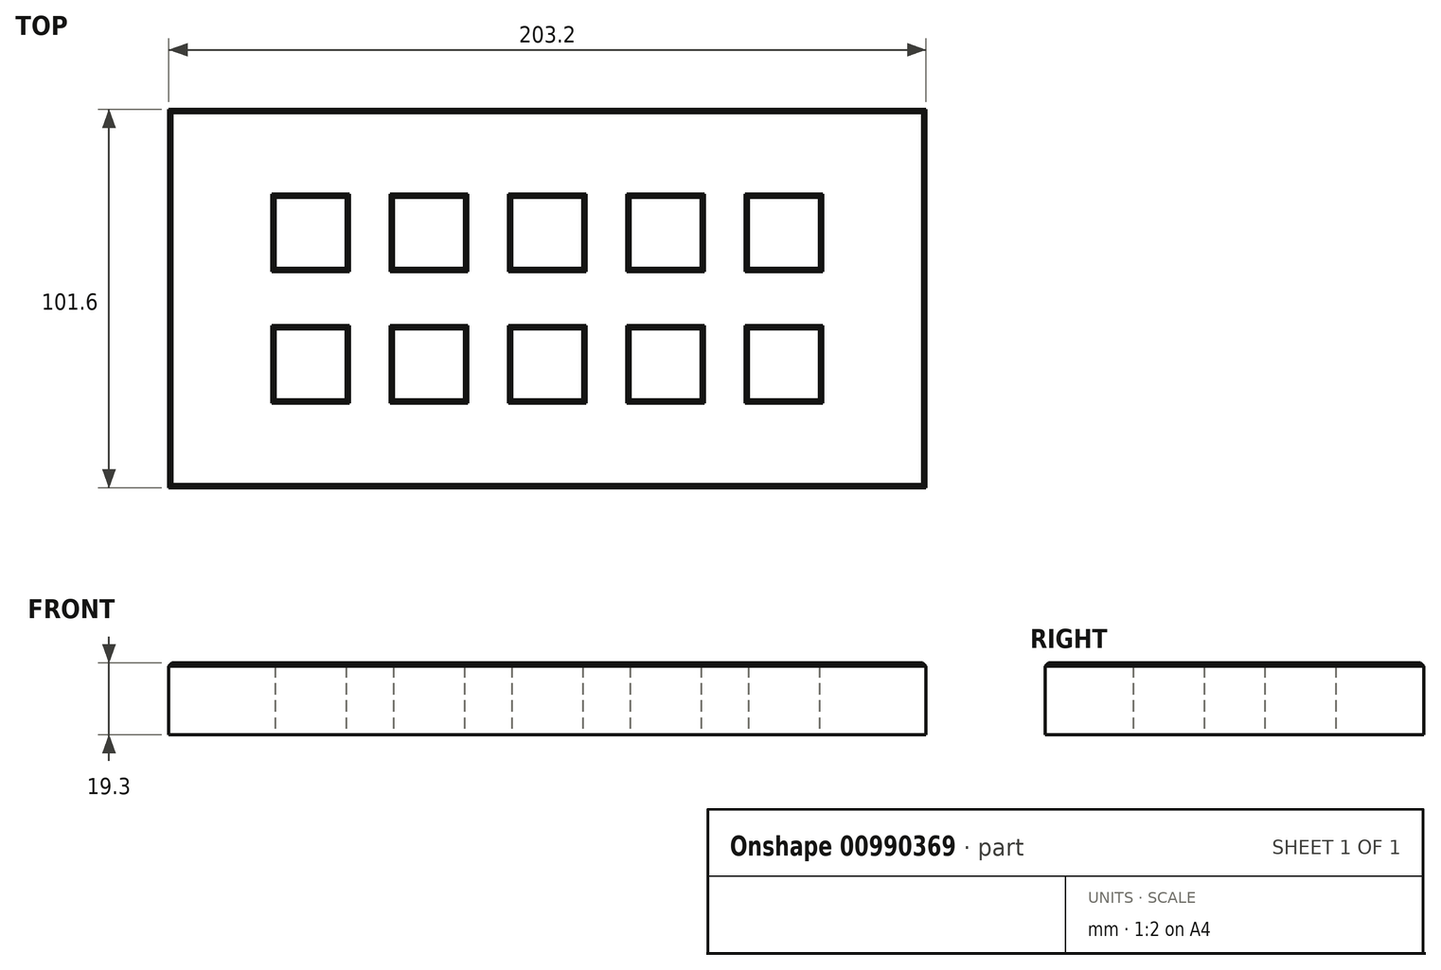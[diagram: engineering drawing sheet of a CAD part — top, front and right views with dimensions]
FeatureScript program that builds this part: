
annotation { "Feature Type Name" : "Feature", "Feature Type Description" : "" }
export const myFeature = defineFeature(function(context is Context, id is Id, definition is map)
    precondition{}
    {
        {
            var Q0;
            Q0=qCreatedBy(makeId("Top.planeOp"),FACE);
            var sketch = newSketch(context, id + "F0", { "sketchPlane" : qUnion([Q0])});
            skLineSegment(sketch, "E0.bottom", {"start": v(-101.6, 50.8) * mm, "end": v(101.6, 50.8) * mm});
            skLineSegment(sketch, "E0.top", {"start": v(-101.6, -50.8) * mm, "end": v(101.6, -50.8) * mm});
            skLineSegment(sketch, "E0.left", {"start": v(-101.6, 50.8) * mm, "end": v(-101.6, -50.8) * mm});
            skLineSegment(sketch, "E0.right", {"start": v(101.6, 50.8) * mm, "end": v(101.6, -50.8) * mm});
            skPoint(sketch, "E0.middle", {"position": v(0, 0) * mm});
            skLineSegment(sketch, "E1.bottom", {"start": v(-73.02, 27.17) * mm, "end": v(-53.98, 27.17) * mm});
            skLineSegment(sketch, "E1.top", {"start": v(-73.02, 8.12) * mm, "end": v(-53.97, 8.12) * mm});
            skLineSegment(sketch, "E1.left", {"start": v(-73.02, 27.17) * mm, "end": v(-73.02, 8.12) * mm});
            skLineSegment(sketch, "E1.right", {"start": v(-53.98, 27.17) * mm, "end": v(-53.97, 8.12) * mm});
            skPoint(sketch, "E1.middle", {"position": v(-63.5, 17.65) * mm});
            skLineSegment(sketch, "E2.bottom", {"start": v(-41.27, 8.12) * mm, "end": v(-22.22, 8.12) * mm});
            skLineSegment(sketch, "E2.top", {"start": v(-41.27, 27.17) * mm, "end": v(-22.22, 27.17) * mm});
            skLineSegment(sketch, "E2.left", {"start": v(-41.27, 8.12) * mm, "end": v(-41.27, 27.17) * mm});
            skLineSegment(sketch, "E2.right", {"start": v(-22.22, 8.12) * mm, "end": v(-22.22, 27.17) * mm});
            skLineSegment(sketch, "E3.bottom", {"start": v(-9.52, 8.12) * mm, "end": v(9.53, 8.12) * mm});
            skLineSegment(sketch, "E3.top", {"start": v(-9.52, 27.17) * mm, "end": v(9.53, 27.17) * mm});
            skLineSegment(sketch, "E3.left", {"start": v(-9.52, 8.12) * mm, "end": v(-9.52, 27.17) * mm});
            skLineSegment(sketch, "E3.right", {"start": v(9.53, 8.12) * mm, "end": v(9.53, 27.17) * mm});
            skLineSegment(sketch, "E4.bottom", {"start": v(22.23, 8.12) * mm, "end": v(41.28, 8.12) * mm});
            skLineSegment(sketch, "E4.top", {"start": v(22.23, 27.17) * mm, "end": v(41.28, 27.17) * mm});
            skLineSegment(sketch, "E4.left", {"start": v(22.23, 8.12) * mm, "end": v(22.23, 27.17) * mm});
            skLineSegment(sketch, "E4.right", {"start": v(41.28, 8.12) * mm, "end": v(41.28, 27.17) * mm});
            skLineSegment(sketch, "E5.bottom", {"start": v(53.98, 8.12) * mm, "end": v(73.03, 8.12) * mm});
            skLineSegment(sketch, "E5.top", {"start": v(53.98, 27.17) * mm, "end": v(73.03, 27.17) * mm});
            skLineSegment(sketch, "E5.left", {"start": v(53.98, 8.12) * mm, "end": v(53.98, 27.17) * mm});
            skLineSegment(sketch, "E5.right", {"start": v(73.03, 8.12) * mm, "end": v(73.03, 27.17) * mm});
            skLineSegment(sketch, "E6", {"start": v(0, 0) * mm, "end": v(-101.6, 0) * mm, "construction": true});
            skPoint(sketch, "E7", {"position": v(0, 27.17) * mm});
            skPoint(sketch, "E8", {"position": v(0, 50.8) * mm});
            skPoint(sketch, "E9.MirrorP", {"position": v(0, -27.17) * mm});
            skLineSegment(sketch, "E10.MirrorCS", {"start": v(-73.02, -27.17) * mm, "end": v(-53.98, -27.17) * mm});
            skLineSegment(sketch, "E11.MirrorCS", {"start": v(-73.02, -27.17) * mm, "end": v(-73.02, -8.12) * mm});
            skLineSegment(sketch, "E12.MirrorCS", {"start": v(-73.02, -8.12) * mm, "end": v(-53.97, -8.12) * mm});
            skLineSegment(sketch, "E13.MirrorCS", {"start": v(-53.97, -27.17) * mm, "end": v(-53.97, -8.12) * mm});
            skLineSegment(sketch, "E14.MirrorCS", {"start": v(-41.27, -8.12) * mm, "end": v(-41.27, -27.17) * mm});
            skLineSegment(sketch, "E15.MirrorCS", {"start": v(-41.27, -27.17) * mm, "end": v(-22.22, -27.17) * mm});
            skLineSegment(sketch, "E16.MirrorCS", {"start": v(-22.22, -8.12) * mm, "end": v(-22.22, -27.17) * mm});
            skLineSegment(sketch, "E17.MirrorCS", {"start": v(-41.27, -8.12) * mm, "end": v(-22.22, -8.12) * mm});
            skLineSegment(sketch, "E18.MirrorCS", {"start": v(-9.52, -8.12) * mm, "end": v(-9.52, -27.17) * mm});
            skLineSegment(sketch, "E19.MirrorCS", {"start": v(-9.52, -27.17) * mm, "end": v(9.53, -27.17) * mm});
            skLineSegment(sketch, "E20.MirrorCS", {"start": v(9.53, -8.12) * mm, "end": v(9.53, -27.17) * mm});
            skLineSegment(sketch, "E21.MirrorCS", {"start": v(-9.52, -8.12) * mm, "end": v(9.53, -8.12) * mm});
            skLineSegment(sketch, "E22.MirrorCS", {"start": v(22.23, -8.12) * mm, "end": v(22.23, -27.17) * mm});
            skLineSegment(sketch, "E23.MirrorCS", {"start": v(22.23, -27.17) * mm, "end": v(41.28, -27.17) * mm});
            skLineSegment(sketch, "E24.MirrorCS", {"start": v(41.28, -8.12) * mm, "end": v(41.28, -27.17) * mm});
            skLineSegment(sketch, "E25.MirrorCS", {"start": v(22.23, -8.12) * mm, "end": v(41.28, -8.12) * mm});
            skLineSegment(sketch, "E26.MirrorCS", {"start": v(53.98, -8.12) * mm, "end": v(53.98, -27.17) * mm});
            skLineSegment(sketch, "E27.MirrorCS", {"start": v(53.98, -27.17) * mm, "end": v(73.03, -27.17) * mm});
            skLineSegment(sketch, "E28.MirrorCS", {"start": v(73.03, -8.12) * mm, "end": v(73.03, -27.17) * mm});
            skLineSegment(sketch, "E29.MirrorCS", {"start": v(53.98, -8.12) * mm, "end": v(73.03, -8.12) * mm});
            skSolve(sketch);
        }
        {
            var Q0;
            Q0=makeQuery(id+"F0.imprint","IMPRINT",FACE,{"disambiguationData":[TD([[makeQuery(id+"F0.imprint","IMPRINT",EDGE,{"derivedFrom":sQuery(id+"F0.wireOp",EDGE,"E0.bottom")}),-1.0]])]});
            extrude(context, id + "F1", {"entities" : qUnion([Q0]), "depth" : 19.3 * mm, "offsetDistance" : 25.4 * mm});
        }
        {
            var Q0;
            Q0=makeQuery(id+"F0.imprint","IMPRINT",FACE,{"disambiguationData":[TD([[makeQuery(id+"F0.imprint","IMPRINT",EDGE,{"derivedFrom":sQuery(id+"F0.wireOp",EDGE,"E1.bottom")}),-1.0]])]});
            var Q1;
            Q1=makeQuery(id+"F0.imprint","IMPRINT",FACE,{"disambiguationData":[TD([[makeQuery(id+"F0.imprint","IMPRINT",EDGE,{"derivedFrom":sQuery(id+"F0.wireOp",EDGE,"E2.bottom")}),1.0]])]});
            var Q2;
            Q2=makeQuery(id+"F0.imprint","IMPRINT",FACE,{"disambiguationData":[TD([[makeQuery(id+"F0.imprint","IMPRINT",EDGE,{"derivedFrom":sQuery(id+"F0.wireOp",EDGE,"E3.bottom")}),1.0]])]});
            var Q3;
            Q3=makeQuery(id+"F0.imprint","IMPRINT",FACE,{"disambiguationData":[TD([[makeQuery(id+"F0.imprint","IMPRINT",EDGE,{"derivedFrom":sQuery(id+"F0.wireOp",EDGE,"E4.bottom")}),1.0]])]});
            var Q4;
            Q4=makeQuery(id+"F0.imprint","IMPRINT",FACE,{"disambiguationData":[TD([[makeQuery(id+"F0.imprint","IMPRINT",EDGE,{"derivedFrom":sQuery(id+"F0.wireOp",EDGE,"E5.bottom")}),1.0]])]});
            var Q5;
            Q5=makeQuery(id+"F0.imprint","IMPRINT",FACE,{"disambiguationData":[TD([[makeQuery(id+"F0.imprint","IMPRINT",EDGE,{"derivedFrom":sQuery(id+"F0.wireOp",EDGE,"E26.MirrorCS")}),1.0]])]});
            var Q6;
            Q6=makeQuery(id+"F0.imprint","IMPRINT",FACE,{"disambiguationData":[TD([[makeQuery(id+"F0.imprint","IMPRINT",EDGE,{"derivedFrom":sQuery(id+"F0.wireOp",EDGE,"E22.MirrorCS")}),1.0]])]});
            var Q7;
            Q7=makeQuery(id+"F0.imprint","IMPRINT",FACE,{"disambiguationData":[TD([[makeQuery(id+"F0.imprint","IMPRINT",EDGE,{"derivedFrom":sQuery(id+"F0.wireOp",EDGE,"E18.MirrorCS")}),1.0]])]});
            var Q8;
            Q8=makeQuery(id+"F0.imprint","IMPRINT",FACE,{"disambiguationData":[TD([[makeQuery(id+"F0.imprint","IMPRINT",EDGE,{"derivedFrom":sQuery(id+"F0.wireOp",EDGE,"E14.MirrorCS")}),1.0]])]});
            var Q9;
            Q9=makeQuery(id+"F0.imprint","IMPRINT",FACE,{"disambiguationData":[TD([[makeQuery(id+"F0.imprint","IMPRINT",EDGE,{"derivedFrom":sQuery(id+"F0.wireOp",EDGE,"E10.MirrorCS")}),1.0]])]});
            extrude(context, id + "F2", {"entities" : qUnion([Q0, Q1, Q2, Q3, Q4, Q5, Q6, Q7, Q8, Q9]), "depth" : 19.3 * mm, "offsetDistance" : 25.4 * mm});
        }
        {
            var Q0;
            Q0=makeQuery(id+"F2.opExtrude","CAP_FACE",FACE,{"disambiguationData":[OSD([sQuery(id+"F0.wireOp",EDGE,"E1.bottom"),sQuery(id+"F0.wireOp",EDGE,"E1.top"),sQuery(id+"F0.wireOp",EDGE,"E1.left"),sQuery(id+"F0.wireOp",EDGE,"E1.right")])],"isStart":false});
            var Q1;
            Q1=makeQuery(id+"F2.opExtrude","CAP_FACE",FACE,{"disambiguationData":[OSD([sQuery(id+"F0.wireOp",EDGE,"E2.bottom"),sQuery(id+"F0.wireOp",EDGE,"E2.top"),sQuery(id+"F0.wireOp",EDGE,"E2.left"),sQuery(id+"F0.wireOp",EDGE,"E2.right")])],"isStart":false});
            var Q2;
            Q2=makeQuery(id+"F2.opExtrude","CAP_FACE",FACE,{"disambiguationData":[OSD([sQuery(id+"F0.wireOp",EDGE,"E3.bottom"),sQuery(id+"F0.wireOp",EDGE,"E3.top"),sQuery(id+"F0.wireOp",EDGE,"E3.left"),sQuery(id+"F0.wireOp",EDGE,"E3.right")])],"isStart":false});
            var Q3;
            Q3=makeQuery(id+"F2.opExtrude","CAP_FACE",FACE,{"disambiguationData":[OSD([sQuery(id+"F0.wireOp",EDGE,"E4.bottom"),sQuery(id+"F0.wireOp",EDGE,"E4.top"),sQuery(id+"F0.wireOp",EDGE,"E4.left"),sQuery(id+"F0.wireOp",EDGE,"E4.right")])],"isStart":false});
            var Q4;
            Q4=makeQuery(id+"F2.opExtrude","CAP_FACE",FACE,{"disambiguationData":[OSD([sQuery(id+"F0.wireOp",EDGE,"E5.bottom"),sQuery(id+"F0.wireOp",EDGE,"E5.top"),sQuery(id+"F0.wireOp",EDGE,"E5.left"),sQuery(id+"F0.wireOp",EDGE,"E5.right")])],"isStart":false});
            var Q5;
            Q5=makeQuery(id+"F2.opExtrude","CAP_FACE",FACE,{"disambiguationData":[OSD([sQuery(id+"F0.wireOp",EDGE,"E26.MirrorCS"),sQuery(id+"F0.wireOp",EDGE,"E27.MirrorCS"),sQuery(id+"F0.wireOp",EDGE,"E28.MirrorCS"),sQuery(id+"F0.wireOp",EDGE,"E29.MirrorCS")])],"isStart":false});
            var Q6;
            Q6=makeQuery(id+"F2.opExtrude","CAP_FACE",FACE,{"disambiguationData":[OSD([sQuery(id+"F0.wireOp",EDGE,"E22.MirrorCS"),sQuery(id+"F0.wireOp",EDGE,"E23.MirrorCS"),sQuery(id+"F0.wireOp",EDGE,"E24.MirrorCS"),sQuery(id+"F0.wireOp",EDGE,"E25.MirrorCS")])],"isStart":false});
            var Q7;
            Q7=makeQuery(id+"F2.opExtrude","CAP_FACE",FACE,{"disambiguationData":[OSD([sQuery(id+"F0.wireOp",EDGE,"E18.MirrorCS"),sQuery(id+"F0.wireOp",EDGE,"E19.MirrorCS"),sQuery(id+"F0.wireOp",EDGE,"E20.MirrorCS"),sQuery(id+"F0.wireOp",EDGE,"E21.MirrorCS")])],"isStart":false});
            var Q8;
            Q8=makeQuery(id+"F2.opExtrude","CAP_FACE",FACE,{"disambiguationData":[OSD([sQuery(id+"F0.wireOp",EDGE,"E14.MirrorCS"),sQuery(id+"F0.wireOp",EDGE,"E15.MirrorCS"),sQuery(id+"F0.wireOp",EDGE,"E16.MirrorCS"),sQuery(id+"F0.wireOp",EDGE,"E17.MirrorCS")])],"isStart":false});
            var Q9;
            Q9=makeQuery(id+"F2.opExtrude","CAP_FACE",FACE,{"disambiguationData":[OSD([sQuery(id+"F0.wireOp",EDGE,"E10.MirrorCS"),sQuery(id+"F0.wireOp",EDGE,"E11.MirrorCS"),sQuery(id+"F0.wireOp",EDGE,"E12.MirrorCS"),sQuery(id+"F0.wireOp",EDGE,"E13.MirrorCS")])],"isStart":false});
            extrude(context, id + "F3", {"entities" : qUnion([Q0, Q1, Q2, Q3, Q4, Q5, Q6, Q7, Q8, Q9]), "operationType" : NewBodyOperationType.REMOVE, "oppositeDirection" : true, "depth" : 0.89 * mm, "offsetDistance" : 25.4 * mm});
        }
        {
            var Q0;
            Q0=makeQuery(id+"F1.opExtrude","CAP_FACE",FACE,{"disambiguationData":[OSD([sQuery(id+"F0.wireOp",EDGE,"E0.bottom"),sQuery(id+"F0.wireOp",EDGE,"E0.top"),sQuery(id+"F0.wireOp",EDGE,"E0.left"),sQuery(id+"F0.wireOp",EDGE,"E0.right"),sQuery(id+"F0.wireOp",EDGE,"E1.bottom"),sQuery(id+"F0.wireOp",EDGE,"E1.top"),sQuery(id+"F0.wireOp",EDGE,"E1.left"),sQuery(id+"F0.wireOp",EDGE,"E1.right"),sQuery(id+"F0.wireOp",EDGE,"E2.bottom"),sQuery(id+"F0.wireOp",EDGE,"E2.top"),sQuery(id+"F0.wireOp",EDGE,"E2.left"),sQuery(id+"F0.wireOp",EDGE,"E2.right"),sQuery(id+"F0.wireOp",EDGE,"E3.bottom"),sQuery(id+"F0.wireOp",EDGE,"E3.top"),sQuery(id+"F0.wireOp",EDGE,"E3.left"),sQuery(id+"F0.wireOp",EDGE,"E3.right"),sQuery(id+"F0.wireOp",EDGE,"E4.bottom"),sQuery(id+"F0.wireOp",EDGE,"E4.top"),sQuery(id+"F0.wireOp",EDGE,"E4.left"),sQuery(id+"F0.wireOp",EDGE,"E4.right"),sQuery(id+"F0.wireOp",EDGE,"E5.bottom"),sQuery(id+"F0.wireOp",EDGE,"E5.top"),sQuery(id+"F0.wireOp",EDGE,"E5.left"),sQuery(id+"F0.wireOp",EDGE,"E5.right"),sQuery(id+"F0.wireOp",EDGE,"E10.MirrorCS"),sQuery(id+"F0.wireOp",EDGE,"E11.MirrorCS"),sQuery(id+"F0.wireOp",EDGE,"E12.MirrorCS"),sQuery(id+"F0.wireOp",EDGE,"E13.MirrorCS"),sQuery(id+"F0.wireOp",EDGE,"E14.MirrorCS"),sQuery(id+"F0.wireOp",EDGE,"E15.MirrorCS"),sQuery(id+"F0.wireOp",EDGE,"E16.MirrorCS"),sQuery(id+"F0.wireOp",EDGE,"E17.MirrorCS"),sQuery(id+"F0.wireOp",EDGE,"E18.MirrorCS"),sQuery(id+"F0.wireOp",EDGE,"E19.MirrorCS"),sQuery(id+"F0.wireOp",EDGE,"E20.MirrorCS"),sQuery(id+"F0.wireOp",EDGE,"E21.MirrorCS"),sQuery(id+"F0.wireOp",EDGE,"E22.MirrorCS"),sQuery(id+"F0.wireOp",EDGE,"E23.MirrorCS"),sQuery(id+"F0.wireOp",EDGE,"E24.MirrorCS"),sQuery(id+"F0.wireOp",EDGE,"E25.MirrorCS"),sQuery(id+"F0.wireOp",EDGE,"E26.MirrorCS"),sQuery(id+"F0.wireOp",EDGE,"E27.MirrorCS"),sQuery(id+"F0.wireOp",EDGE,"E28.MirrorCS"),sQuery(id+"F0.wireOp",EDGE,"E29.MirrorCS")])],"isStart":false});
            chamfer(context, id + "F4", {"entities" : qUnion([Q0]), "width" : 0.89 * mm, "tangentPropagation" : true});
        }
    });
